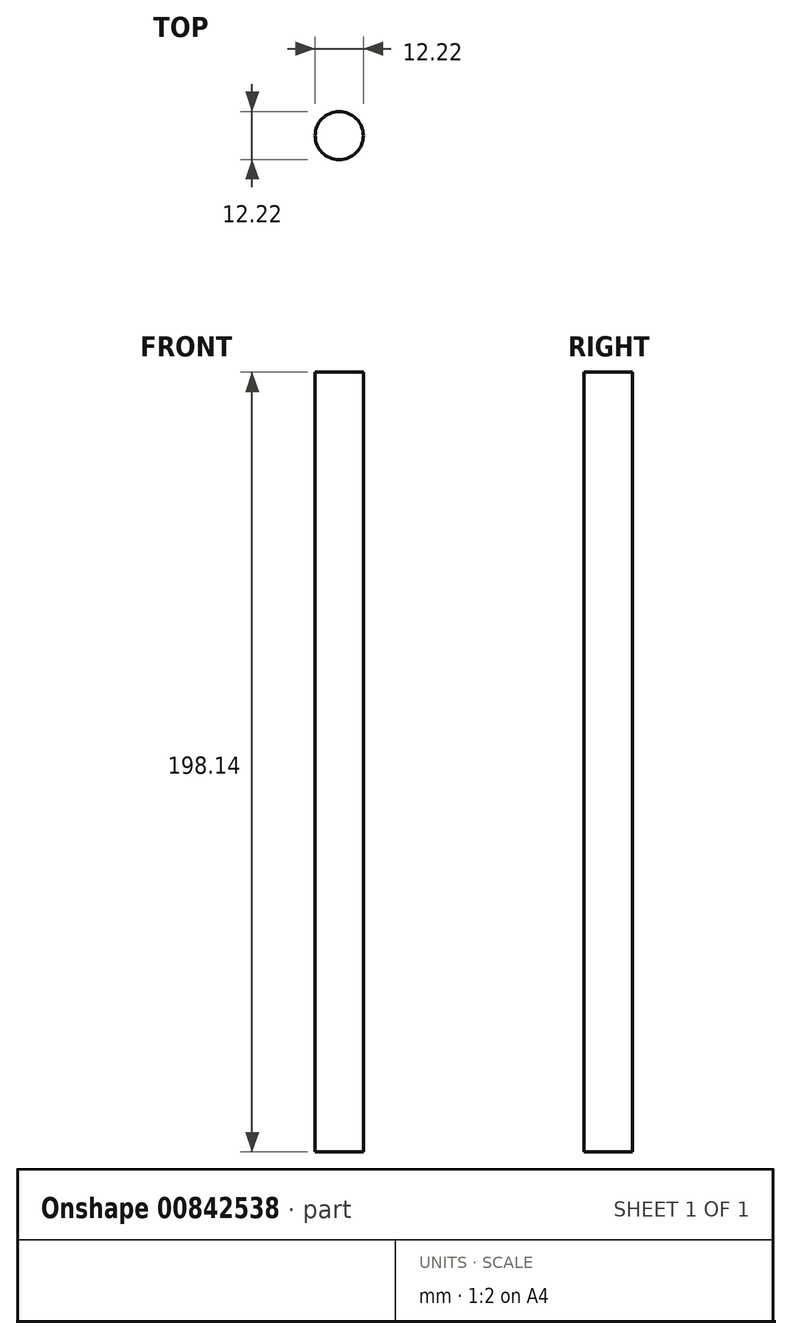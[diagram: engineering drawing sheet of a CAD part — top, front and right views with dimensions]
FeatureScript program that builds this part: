
annotation { "Feature Type Name" : "Feature", "Feature Type Description" : "" }
export const myFeature = defineFeature(function(context is Context, id is Id, definition is map)
    precondition{}
    {
        {
            var Q0;
            Q0=qCreatedBy(makeId("Top.planeOp"),FACE);
            var sketch = newSketch(context, id + "F0", { "sketchPlane" : qUnion([Q0])});
            skCircle(sketch, "E0", {"center": v(0, 0) * mm, "radius": 6.11 * mm});
            skSolve(sketch);
        }
        {
            var Q0;
            Q0 = qSketchRegion(id + "F0", true);
            extrude(context, id + "F1", {"entities" : qUnion([Q0]), "depth" : 198.14 * mm, "offsetDistance" : 25.4 * mm});
        }
    });
